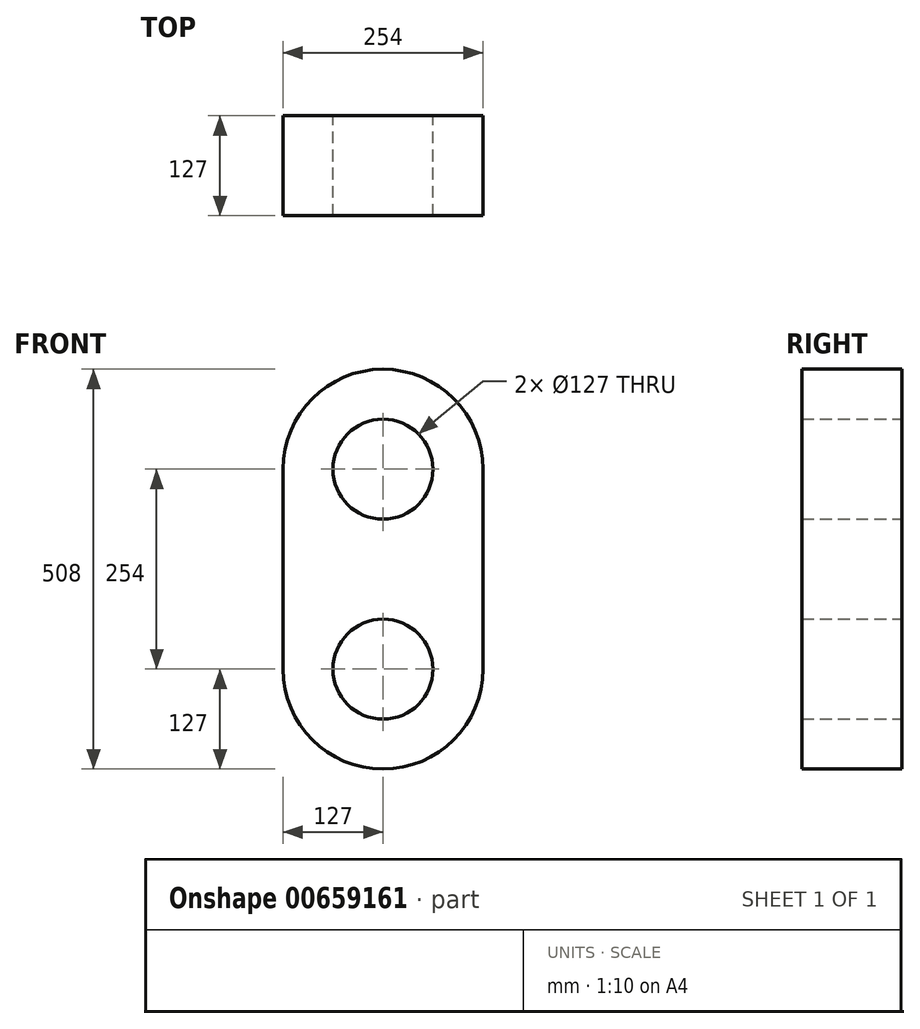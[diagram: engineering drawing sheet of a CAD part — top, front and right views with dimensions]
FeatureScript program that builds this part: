
annotation { "Feature Type Name" : "Feature", "Feature Type Description" : "" }
export const myFeature = defineFeature(function(context is Context, id is Id, definition is map)
    precondition{}
    {
        {
            var Q0;
            Q0=qCreatedBy(makeId("Front.planeOp"),FACE);
            var sketch = newSketch(context, id + "F0", { "sketchPlane" : qUnion([Q0])});
            skLineSegment(sketch, "E0.left", {"start": v(-127, 127) * mm, "end": v(-127, -127) * mm});
            skLineSegment(sketch, "E0.right", {"start": v(127, 127) * mm, "end": v(127, -127) * mm});
            skPoint(sketch, "E0.middle", {"position": v(0, 0) * mm});
            skArc(sketch, "E1", {"start": v(127, 127) * mm, "mid": v(0, 254) * mm, "end": v(-127, 127) * mm});
            skPoint(sketch, "E2.orphan", {"position": v(-127, 254) * mm});
            skPoint(sketch, "E3.orphan", {"position": v(127, 254) * mm});
            skCircle(sketch, "E4", {"center": v(0, 127) * mm, "radius": 63.5 * mm});
            skArc(sketch, "E5", {"start": v(-127, -127) * mm, "mid": v(0, -254) * mm, "end": v(127, -127) * mm});
            skPoint(sketch, "E6.orphan", {"position": v(-127, -254) * mm});
            skPoint(sketch, "E7.orphan", {"position": v(127, -254) * mm});
            skCircle(sketch, "E8", {"center": v(0, -127) * mm, "radius": 63.5 * mm});
            skSolve(sketch);
        }
        {
            var Q0;
            Q0=makeQuery(id+"F0.imprint","IMPRINT",FACE,{"disambiguationData":[TD([[makeQuery(id+"F0.imprint","IMPRINT",EDGE,{"derivedFrom":sQuery(id+"F0.wireOp",EDGE,"E0.left")}),1.0]])]});
            extrude(context, id + "F1", {"entities" : qUnion([Q0]), "depth" : 127 * mm, "offsetDistance" : 25.4 * mm});
        }
    });
